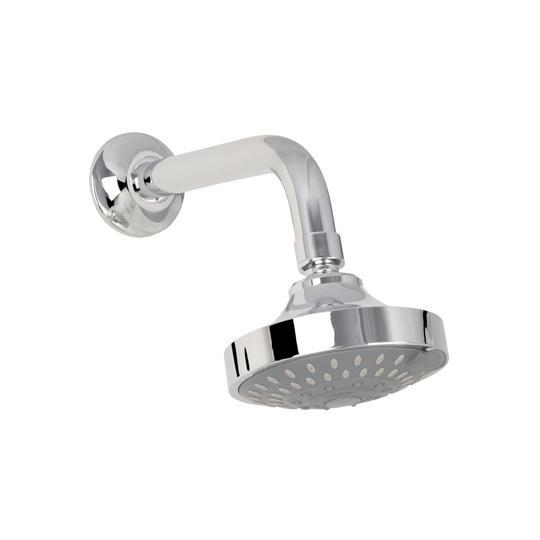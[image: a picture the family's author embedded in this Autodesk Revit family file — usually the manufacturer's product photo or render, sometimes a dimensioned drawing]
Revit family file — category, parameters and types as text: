
# Revit family: 01-1735-11 MEZCLADOR DUCHA 8 SST HELIX PALA
name_source: partatom
category: Aparatos sanitarios
revit_build: Autodesk Revit 2018 (Build: 20170223_1515(x64)
units: mm (PartAtom-declared; Revit-internal decimal feet)

## family parameters
Anfitrión = Cara
Compartido = No
Corte con vacíos al cargar = No
Cota de conector redondo = Diámetro de uso
Número OmniClass = 23.31.11.00
Punto de cálculo de habitación = No
Tipo de pieza = Normal

## types (1)
- 01-1735-11
    Alto = 60 mm  [stored 0.19685 ft]
    Ancho = 60 mm  [stored 0.19685 ft]
    Conexión AC = Sí
    Conexión AF = Sí
    Conexión de residuos = No
    Conexión de ventilación = No
    Descripción = Mezclador ducha
    Distancia entre griferias = 203 mm
    Elevación por defecto = 0 mm  [stored 0 ft]
    Fabricante = Gricol
    Imagen de tipo = <Ninguno>
    Link Ficha Tecnica = https://infotecnica.gricol.com
    Modelo = 01-1735-11
    Plastico ABS Cromado = Plastico ABS Cromado
    Product Name = MEZCLADOR DUCHA 8 SST HELIX PALA
    Profundidad = 85 mm  [stored 0.278871 ft]
    Sepacion entre registro y ducha = 400 mm  [stored 1.31234 ft]
    URL = https://www.gricol.com

note: [stored X ft] marks values corroborated as IEEE doubles in the binary element streams (Revit-internal decimal feet)

## geometry (parser evidence)
native form markers: Blend x2, Sweep x32
no freeform markers — native parametric forms only
